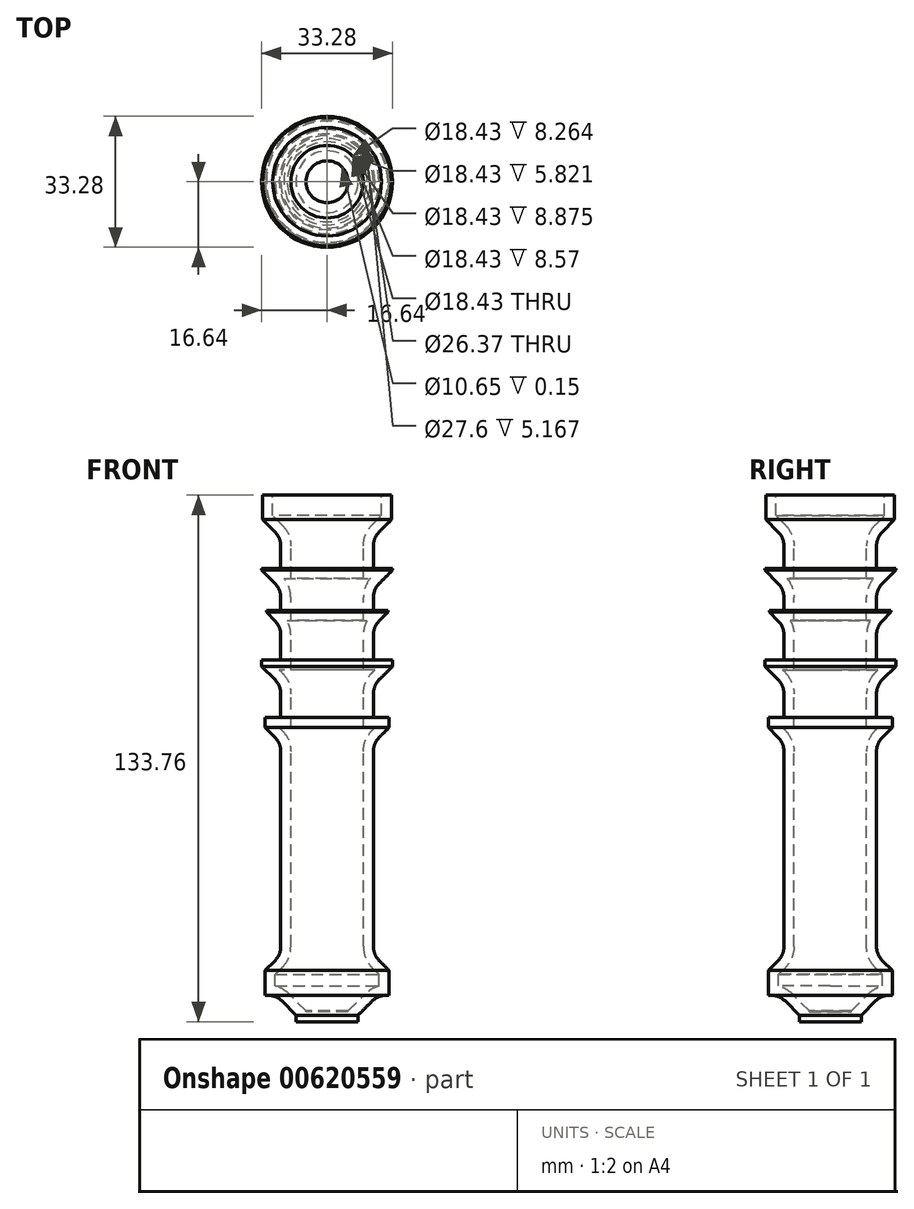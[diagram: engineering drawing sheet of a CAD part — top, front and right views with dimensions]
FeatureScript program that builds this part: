
annotation { "Feature Type Name" : "Feature", "Feature Type Description" : "" }
export const myFeature = defineFeature(function(context is Context, id is Id, definition is map)
    precondition{}
    {
        {
            var Q0;
            Q0=qCreatedBy(makeId("Front.planeOp"),FACE);
            var sketch = newSketch(context, id + "F0", { "sketchPlane" : qUnion([Q0])});
            skLineSegment(sketch, "E0.bottom", {"start": v(0, 75.58) * mm, "end": v(-16.34, 75.58) * mm});
            skLineSegment(sketch, "E0.top", {"start": v(0, 64.28) * mm, "end": v(-16.34, 64.28) * mm});
            skLineSegment(sketch, "E0.left", {"start": v(0, 75.58) * mm, "end": v(0, 64.28) * mm});
            skLineSegment(sketch, "E0.right", {"start": v(-16.34, 75.58) * mm, "end": v(-16.34, 64.28) * mm});
            skLineSegment(sketch, "E1.bottom", {"start": v(0, 64.28) * mm, "end": v(-11.76, 64.28) * mm});
            skLineSegment(sketch, "E1.top", {"start": v(0, 56.95) * mm, "end": v(-11.76, 56.95) * mm});
            skLineSegment(sketch, "E1.left", {"start": v(0, 64.28) * mm, "end": v(0, 56.95) * mm});
            skLineSegment(sketch, "E1.right", {"start": v(-11.76, 64.28) * mm, "end": v(-11.76, 56.95) * mm});
            skLineSegment(sketch, "E2.bottom", {"start": v(0, 56.95) * mm, "end": v(-16.64, 56.95) * mm});
            skLineSegment(sketch, "E2.top", {"start": v(0, 51.46) * mm, "end": v(-16.64, 51.46) * mm});
            skLineSegment(sketch, "E2.left", {"start": v(0, 56.95) * mm, "end": v(0, 51.46) * mm});
            skLineSegment(sketch, "E2.right", {"start": v(-16.64, 56.95) * mm, "end": v(-16.64, 51.46) * mm});
            skLineSegment(sketch, "E3.bottom", {"start": v(0, 51.46) * mm, "end": v(-11.76, 51.46) * mm});
            skLineSegment(sketch, "E3.top", {"start": v(0, 46.27) * mm, "end": v(-11.76, 46.27) * mm});
            skLineSegment(sketch, "E3.left", {"start": v(0, 51.46) * mm, "end": v(0, 46.27) * mm});
            skLineSegment(sketch, "E3.right", {"start": v(-11.76, 51.46) * mm, "end": v(-11.76, 46.27) * mm});
            skLineSegment(sketch, "E4.bottom", {"start": v(0, 46.27) * mm, "end": v(-15.42, 46.27) * mm});
            skLineSegment(sketch, "E4.top", {"start": v(0, 40.77) * mm, "end": v(-15.42, 40.77) * mm});
            skLineSegment(sketch, "E4.left", {"start": v(0, 46.27) * mm, "end": v(0, 40.77) * mm});
            skLineSegment(sketch, "E4.right", {"start": v(-15.42, 46.27) * mm, "end": v(-15.42, 40.77) * mm});
            skLineSegment(sketch, "E5.bottom", {"start": v(0, 40.77) * mm, "end": v(-11.76, 40.77) * mm});
            skLineSegment(sketch, "E5.top", {"start": v(0, 33.74) * mm, "end": v(-11.76, 33.74) * mm});
            skLineSegment(sketch, "E5.left", {"start": v(0, 40.77) * mm, "end": v(0, 33.74) * mm});
            skLineSegment(sketch, "E5.right", {"start": v(-11.76, 40.77) * mm, "end": v(-11.76, 33.74) * mm});
            skLineSegment(sketch, "E6.bottom", {"start": v(0, 33.74) * mm, "end": v(-16.64, 33.74) * mm});
            skLineSegment(sketch, "E6.top", {"start": v(0, 27.03) * mm, "end": v(-16.64, 27.03) * mm});
            skLineSegment(sketch, "E6.left", {"start": v(0, 33.74) * mm, "end": v(0, 27.03) * mm});
            skLineSegment(sketch, "E6.right", {"start": v(-16.64, 33.74) * mm, "end": v(-16.64, 27.03) * mm});
            skLineSegment(sketch, "E7.bottom", {"start": v(0, 27.03) * mm, "end": v(-11.76, 27.03) * mm});
            skLineSegment(sketch, "E7.top", {"start": v(0, 19.09) * mm, "end": v(-11.76, 19.09) * mm});
            skLineSegment(sketch, "E7.left", {"start": v(0, 27.03) * mm, "end": v(0, 19.09) * mm});
            skLineSegment(sketch, "E7.right", {"start": v(-11.76, 27.03) * mm, "end": v(-11.76, 19.09) * mm});
            skLineSegment(sketch, "E8.bottom", {"start": v(0, 19.09) * mm, "end": v(-15.73, 19.09) * mm});
            skLineSegment(sketch, "E8.top", {"start": v(0, 11.45) * mm, "end": v(-15.73, 11.45) * mm});
            skLineSegment(sketch, "E8.left", {"start": v(0, 19.09) * mm, "end": v(0, 11.45) * mm});
            skLineSegment(sketch, "E8.right", {"start": v(-15.73, 19.09) * mm, "end": v(-15.73, 11.45) * mm});
            skLineSegment(sketch, "E9.bottom", {"start": v(0, 11.45) * mm, "end": v(-11.76, 11.45) * mm});
            skLineSegment(sketch, "E9.top", {"start": v(0, -46.27) * mm, "end": v(-11.76, -46.27) * mm});
            skLineSegment(sketch, "E9.left", {"start": v(0, 11.45) * mm, "end": v(0, -46.27) * mm});
            skLineSegment(sketch, "E9.right", {"start": v(-11.76, 11.45) * mm, "end": v(-11.76, -46.27) * mm});
            skLineSegment(sketch, "E10.bottom", {"start": v(0, -46.27) * mm, "end": v(-15.73, -46.27) * mm});
            skLineSegment(sketch, "E10.top", {"start": v(0, -51.46) * mm, "end": v(-15.73, -51.46) * mm});
            skLineSegment(sketch, "E10.left", {"start": v(0, -46.27) * mm, "end": v(0, -51.46) * mm});
            skLineSegment(sketch, "E10.right", {"start": v(-15.73, -46.27) * mm, "end": v(-15.73, -51.46) * mm});
            skPoint(sketch, "E11.oppositeSnap0", {"position": v(-7.86, -51.46) * mm});
            skLineSegment(sketch, "E11.bottom", {"start": v(0, -51.46) * mm, "end": v(-7.86, -51.46) * mm});
            skLineSegment(sketch, "E11.top", {"start": v(0, -58.18) * mm, "end": v(-7.86, -58.18) * mm});
            skLineSegment(sketch, "E11.left", {"start": v(0, -51.46) * mm, "end": v(0, -58.18) * mm});
            skLineSegment(sketch, "E11.right", {"start": v(-7.86, -51.46) * mm, "end": v(-7.86, -58.18) * mm});
            skSolve(sketch);
        }
        {
            var Q0;
            Q0 = qSketchRegion(id + "F0", true);
            var Q1;
            Q1=sQuery(id+"F0.wireOp",EDGE,"E9.left");
            revolve(context, id + "F1", {"entities" : qUnion([Q0]), "axis" : qUnion([Q1]), "revolveType" : RevolveType.FULL});
        }
        {
            var Q0;
            Q0=makeQuery(id+"F1.opRevolve","SWEPT_EDGE",EDGE,{"disambiguationData":[OSD([sQuery(id+"F0.wireOp",EDGE,"E8.top"),sQuery(id+"F0.wireOp",EDGE,"E8.right")])]});
            var Q1;
            Q1=makeQuery(id+"F1.opRevolve","SWEPT_EDGE",EDGE,{"disambiguationData":[OSD([sQuery(id+"F0.wireOp",EDGE,"E6.top"),sQuery(id+"F0.wireOp",EDGE,"E6.right")])]});
            var Q2;
            Q2=makeQuery(id+"F1.opRevolve","SWEPT_EDGE",EDGE,{"disambiguationData":[OSD([sQuery(id+"F0.wireOp",EDGE,"E4.top"),sQuery(id+"F0.wireOp",EDGE,"E4.right")])]});
            var Q3;
            Q3=makeQuery(id+"F1.opRevolve","SWEPT_EDGE",EDGE,{"disambiguationData":[OSD([sQuery(id+"F0.wireOp",EDGE,"E2.top"),sQuery(id+"F0.wireOp",EDGE,"E2.right")])]});
            var Q4;
            Q4=makeQuery(id+"F1.opRevolve","SWEPT_EDGE",EDGE,{"disambiguationData":[OSD([sQuery(id+"F0.wireOp",EDGE,"E0.top"),sQuery(id+"F0.wireOp",EDGE,"E0.right")])]});
            var Q5;
            Q5=makeQuery(id+"F1.opRevolve","SWEPT_EDGE",EDGE,{"disambiguationData":[OSD([sQuery(id+"F0.wireOp",EDGE,"E9.right"),sQuery(id+"F0.wireOp",EDGE,"E10.bottom")])]});
            var Q6;
            Q6=makeQuery(id+"F1.opRevolve","SWEPT_EDGE",EDGE,{"disambiguationData":[OSD([sQuery(id+"F0.wireOp",EDGE,"E10.top"),sQuery(id+"F0.wireOp",EDGE,"E11.bottom"),sQuery(id+"F0.wireOp",EDGE,"E11.right")])]});
            chamfer(context, id + "F2", {"entities" : qUnion([Q0, Q1, Q2, Q3, Q4, Q5, Q6]), "width" : 5.08 * mm, "tangentPropagation" : true});
        }
        {
            var Q0;
            Q0=makeQuery(id+"F2.opChamfer","BLEND_EDGE",EDGE,{"blendedFrom":[makeQuery(id+"F1.opRevolve","SWEPT_EDGE",EDGE,{"disambiguationData":[OSD([sQuery(id+"F0.wireOp",EDGE,"E8.top"),sQuery(id+"F0.wireOp",EDGE,"E8.right")])]}),makeQuery(id+"F1.opRevolve","SWEPT_FACE",FACE,{"disambiguationData":[OSD([sQuery(id+"F0.wireOp",EDGE,"E9.right")])]})],"blendedInto":[makeQuery(id+"F1.opRevolve","SWEPT_FACE",FACE,{"disambiguationData":[OSD([sQuery(id+"F0.wireOp",EDGE,"E9.right")])]})]});
            var Q1;
            Q1=makeQuery(id+"F2.opChamfer","BLEND_EDGE",EDGE,{"blendedFrom":[makeQuery(id+"F1.opRevolve","SWEPT_EDGE",EDGE,{"disambiguationData":[OSD([sQuery(id+"F0.wireOp",EDGE,"E6.top"),sQuery(id+"F0.wireOp",EDGE,"E6.right")])]}),makeQuery(id+"F1.opRevolve","SWEPT_FACE",FACE,{"disambiguationData":[OSD([sQuery(id+"F0.wireOp",EDGE,"E7.right")])]})],"blendedInto":[makeQuery(id+"F1.opRevolve","SWEPT_FACE",FACE,{"disambiguationData":[OSD([sQuery(id+"F0.wireOp",EDGE,"E7.right")])]})]});
            var Q2;
            Q2=makeQuery(id+"F2.opChamfer","BLEND_EDGE",EDGE,{"blendedFrom":[makeQuery(id+"F1.opRevolve","SWEPT_EDGE",EDGE,{"disambiguationData":[OSD([sQuery(id+"F0.wireOp",EDGE,"E4.top"),sQuery(id+"F0.wireOp",EDGE,"E4.right")])]}),makeQuery(id+"F1.opRevolve","SWEPT_FACE",FACE,{"disambiguationData":[OSD([sQuery(id+"F0.wireOp",EDGE,"E5.right")])]})],"blendedInto":[makeQuery(id+"F1.opRevolve","SWEPT_FACE",FACE,{"disambiguationData":[OSD([sQuery(id+"F0.wireOp",EDGE,"E5.right")])]})]});
            var Q3;
            Q3=makeQuery(id+"F2.opChamfer","BLEND_EDGE",EDGE,{"blendedFrom":[makeQuery(id+"F1.opRevolve","SWEPT_EDGE",EDGE,{"disambiguationData":[OSD([sQuery(id+"F0.wireOp",EDGE,"E2.top"),sQuery(id+"F0.wireOp",EDGE,"E2.right")])]}),makeQuery(id+"F1.opRevolve","SWEPT_FACE",FACE,{"disambiguationData":[OSD([sQuery(id+"F0.wireOp",EDGE,"E3.right")])]})],"blendedInto":[makeQuery(id+"F1.opRevolve","SWEPT_FACE",FACE,{"disambiguationData":[OSD([sQuery(id+"F0.wireOp",EDGE,"E3.right")])]})]});
            var Q4;
            Q4=makeQuery(id+"F2.opChamfer","BLEND_EDGE",EDGE,{"blendedFrom":[makeQuery(id+"F1.opRevolve","SWEPT_EDGE",EDGE,{"disambiguationData":[OSD([sQuery(id+"F0.wireOp",EDGE,"E0.top"),sQuery(id+"F0.wireOp",EDGE,"E0.right")])]}),makeQuery(id+"F1.opRevolve","SWEPT_FACE",FACE,{"disambiguationData":[OSD([sQuery(id+"F0.wireOp",EDGE,"E1.right")])]})],"blendedInto":[makeQuery(id+"F1.opRevolve","SWEPT_FACE",FACE,{"disambiguationData":[OSD([sQuery(id+"F0.wireOp",EDGE,"E1.right")])]})]});
            var Q5;
            Q5=makeQuery(id+"F1.opRevolve","SWEPT_EDGE",EDGE,{"disambiguationData":[OSD([sQuery(id+"F0.wireOp",EDGE,"E10.top"),sQuery(id+"F0.wireOp",EDGE,"E11.bottom"),sQuery(id+"F0.wireOp",EDGE,"E11.right")])]});
            var Q6;
            Q6=makeQuery(id+"F1.opRevolve","SWEPT_EDGE",EDGE,{"disambiguationData":[OSD([sQuery(id+"F0.wireOp",EDGE,"E9.right"),sQuery(id+"F0.wireOp",EDGE,"E10.bottom")])]});
            fillet(context, id + "F3", {"entities" : qUnion([Q0, Q1, Q2, Q3, Q4, Q5, Q6]), "radius" : 5.08 * mm, "tangentPropagation" : true, "allowEdgeOverflow" : false});
        }
        {
            var Q0;
            {var subQ0=sQuery(id+"F0.wireOp",EDGE,"E9.right");Q0=makeQuery(id+"F2.opChamfer","BLEND_EDGE",EDGE,{"blendedFrom":[makeQuery(id+"F1.opRevolve","SWEPT_EDGE",EDGE,{"disambiguationData":[OSD([subQ0,sQuery(id+"F0.wireOp",EDGE,"E10.bottom")])]}),makeQuery(id+"F1.opRevolve","SWEPT_FACE",FACE,{"disambiguationData":[OSD([subQ0])]})],"blendedInto":[makeQuery(id+"F1.opRevolve","SWEPT_FACE",FACE,{"disambiguationData":[OSD([subQ0])]})]});}
            var Q1;
            {var subQ0=sQuery(id+"F0.wireOp",EDGE,"E10.top");Q1=makeQuery(id+"F2.opChamfer","BLEND_EDGE",EDGE,{"blendedFrom":[makeQuery(id+"F1.opRevolve","SWEPT_EDGE",EDGE,{"disambiguationData":[OSD([subQ0,sQuery(id+"F0.wireOp",EDGE,"E11.bottom"),sQuery(id+"F0.wireOp",EDGE,"E11.right")])]}),makeQuery(id+"F1.opRevolve","SWEPT_FACE",FACE,{"disambiguationData":[OSD([subQ0])]})],"blendedInto":[makeQuery(id+"F1.opRevolve","SWEPT_FACE",FACE,{"disambiguationData":[OSD([subQ0])]})]});}
            fillet(context, id + "F4", {"entities" : qUnion([Q0, Q1]), "radius" : 5.08 * mm, "tangentPropagation" : true, "allowEdgeOverflow" : false});
        }
        {
            var Q0;
            Q0=makeQuery(id+"F1.opRevolve","SWEPT_FACE",FACE,{"disambiguationData":[OSD([sQuery(id+"F0.wireOp",EDGE,"E0.bottom")])]});
            shell(context, id + "F5", {"entities" : qUnion([Q0]), "thickness" : 2.54 * mm});
        }
    });
